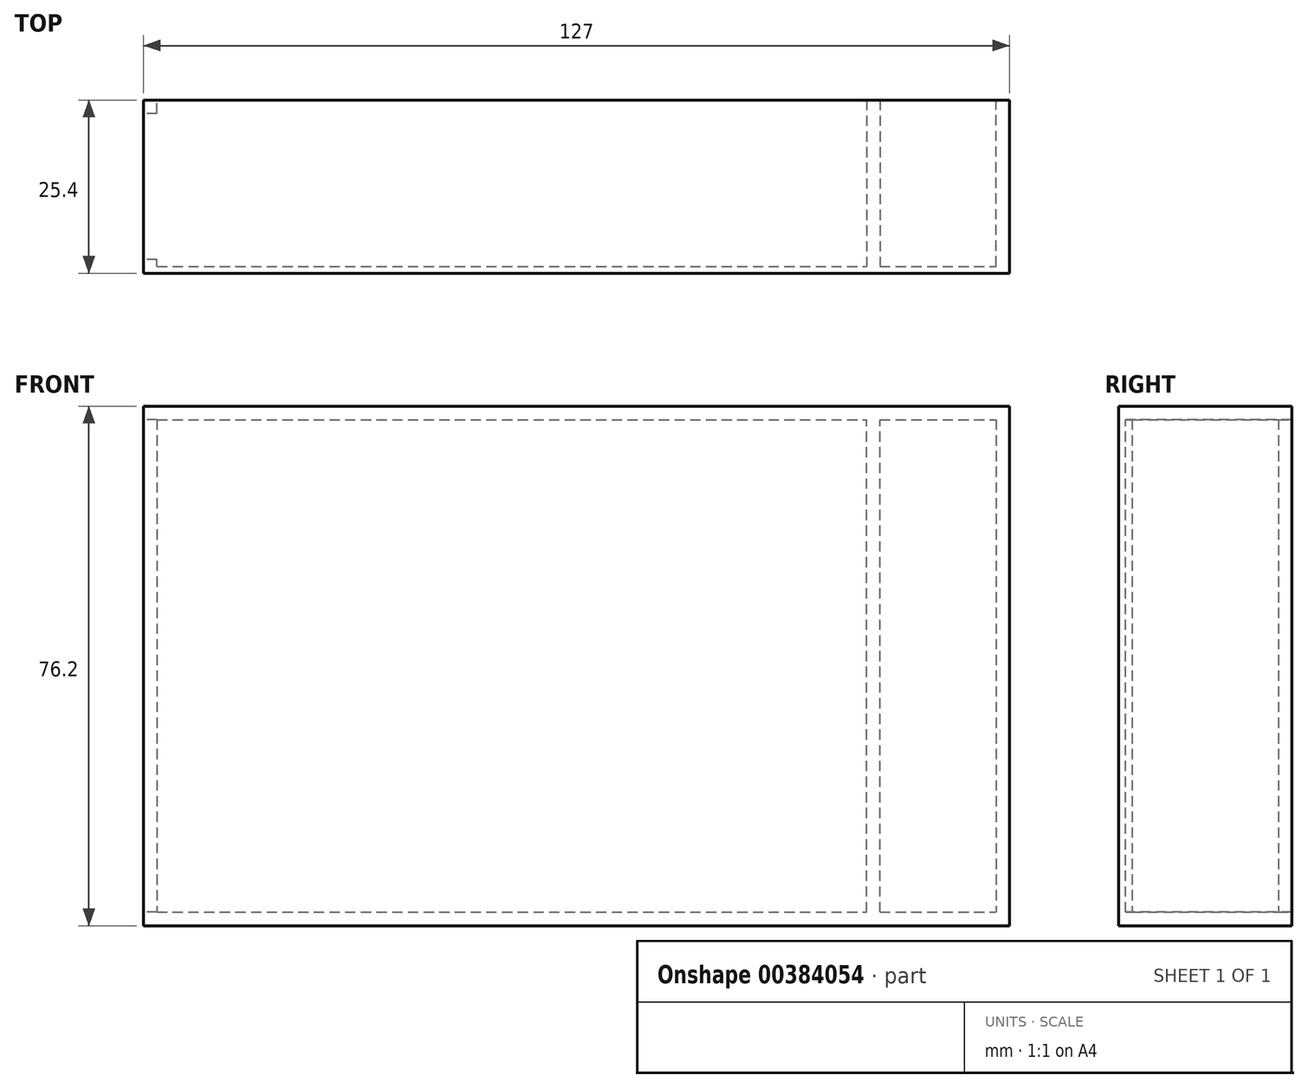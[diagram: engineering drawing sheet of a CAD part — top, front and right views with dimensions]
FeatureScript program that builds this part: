
annotation { "Feature Type Name" : "Feature", "Feature Type Description" : "" }
export const myFeature = defineFeature(function(context is Context, id is Id, definition is map)
    precondition{}
    {
        {
            var Q0;
            Q0=qCreatedBy(makeId("Front.planeOp"),FACE);
            var sketch = newSketch(context, id + "F0", { "sketchPlane" : qUnion([Q0])});
            skLineSegment(sketch, "E0.bottom", {"start": v(-63.5, 38.1) * mm, "end": v(63.5, 38.1) * mm});
            skLineSegment(sketch, "E0.top", {"start": v(-63.5, -38.1) * mm, "end": v(63.5, -38.1) * mm});
            skLineSegment(sketch, "E0.left", {"start": v(-63.5, 38.1) * mm, "end": v(-63.5, -38.1) * mm});
            skLineSegment(sketch, "E0.right", {"start": v(63.5, 38.1) * mm, "end": v(63.5, -38.1) * mm});
            skPoint(sketch, "E0.middle", {"position": v(0, 0) * mm});
            skSolve(sketch);
        }
        {
            var Q0;
            Q0 = qSketchRegion(id + "F0", true);
            extrude(context, id + "F1", {"entities" : qUnion([Q0]), "depth" : 25.4 * mm});
        }
        {
            var Q0;
            Q0=qCreatedBy(makeId("Front.planeOp"),FACE);
            var sketch = newSketch(context, id + "F2", { "sketchPlane" : qUnion([Q0])});
            skLineSegment(sketch, "E1.bottom", {"start": v(-61.52, 36.12) * mm, "end": v(61.52, 36.12) * mm});
            skLineSegment(sketch, "E1.top", {"start": v(-61.52, -36.12) * mm, "end": v(61.52, -36.12) * mm});
            skLineSegment(sketch, "E1.left", {"start": v(-61.52, 36.12) * mm, "end": v(-61.52, -36.12) * mm});
            skLineSegment(sketch, "E1.right", {"start": v(61.52, 36.12) * mm, "end": v(61.52, -36.12) * mm});
            skPoint(sketch, "E1.middle", {"position": v(0, 0) * mm});
            skSolve(sketch);
        }
        {
            var Q0;
            Q0 = qSketchRegion(id + "F2", true);
            extrude(context, id + "F3", {"entities" : qUnion([Q0]), "operationType" : NewBodyOperationType.REMOVE, "depth" : 24.4 * mm});
        }
        {
            var Q0;
            Q0=makeQuery(id+"F3.boolean.opBoolean","COPY",FACE,{"derivedFrom":makeQuery(id+"F3.opExtrude","CAP_FACE",FACE,{"disambiguationData":[OSD([sQuery(id+"F2.wireOp",EDGE,"E1.bottom"),sQuery(id+"F2.wireOp",EDGE,"E1.top"),sQuery(id+"F2.wireOp",EDGE,"E1.left"),sQuery(id+"F2.wireOp",EDGE,"E1.right")])],"isStart":false})});
            var sketch = newSketch(context, id + "F4", { "sketchPlane" : qUnion([Q0])});
            skLineSegment(sketch, "E2.bottom", {"start": v(-44.5, -36.12) * mm, "end": v(-42.52, -36.12) * mm});
            skLineSegment(sketch, "E2.top", {"start": v(-44.5, 36.12) * mm, "end": v(-42.52, 36.12) * mm});
            skLineSegment(sketch, "E2.left", {"start": v(-44.5, -36.12) * mm, "end": v(-44.5, 36.12) * mm});
            skLineSegment(sketch, "E2.right", {"start": v(-42.52, -36.12) * mm, "end": v(-42.52, 36.12) * mm});
            skPoint(sketch, "E3", {"position": v(-61.52, -36.12) * mm});
            skSolve(sketch);
        }
        {
            var Q0;
            Q0 = qSketchRegion(id + "F4", true);
            extrude(context, id + "F5", {"entities" : qUnion([Q0]), "operationType" : NewBodyOperationType.ADD, "depth" : 24.4 * mm});
        }
        {
            var Q0;
            Q0=makeQuery(id+"F1.opExtrude","SWEPT_FACE",FACE,{"disambiguationData":[OSD([sQuery(id+"F0.wireOp",EDGE,"E0.left")])]});
            var sketch = newSketch(context, id + "F6", { "sketchPlane" : qUnion([Q0])});
            skLineSegment(sketch, "E4.bottom", {"start": v(23.42, 36.12) * mm, "end": v(1.98, 36.12) * mm});
            skLineSegment(sketch, "E4.top", {"start": v(23.42, -36.12) * mm, "end": v(1.98, -36.12) * mm});
            skLineSegment(sketch, "E4.left", {"start": v(23.42, 36.12) * mm, "end": v(23.42, -36.12) * mm});
            skLineSegment(sketch, "E4.right", {"start": v(1.98, 36.12) * mm, "end": v(1.98, -36.12) * mm});
            skPoint(sketch, "E5", {"position": v(11.33, 38.1) * mm});
            skPoint(sketch, "E6", {"position": v(25.4, 20.28) * mm});
            skSolve(sketch);
        }
        {
            var Q0;
            Q0=makeQuery(id+"F6.imprint","IMPRINT",FACE,{"disambiguationData":[TD([[makeQuery(id+"F6.imprint","IMPRINT",EDGE,{"derivedFrom":sQuery(id+"F6.wireOp",EDGE,"E4.bottom")}),1.0]])]});
            extrude(context, id + "F7", {"entities" : qUnion([Q0]), "operationType" : NewBodyOperationType.REMOVE, "oppositeDirection" : true, "depth" : 1.98 * mm});
        }
    });
